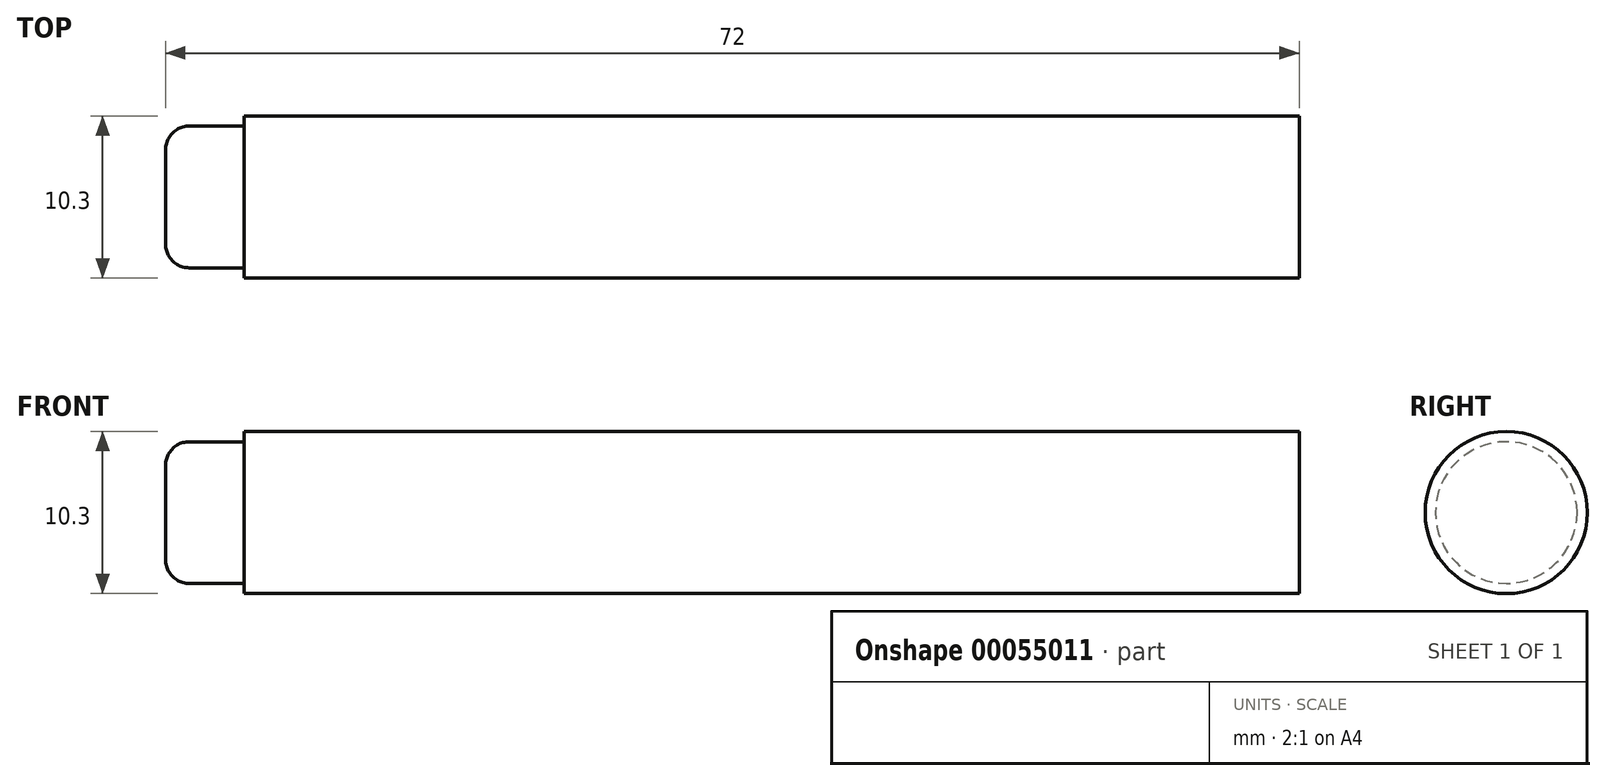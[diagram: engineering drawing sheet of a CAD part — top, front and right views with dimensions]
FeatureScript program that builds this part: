
annotation { "Feature Type Name" : "Feature", "Feature Type Description" : "" }
export const myFeature = defineFeature(function(context is Context, id is Id, definition is map)
    precondition{}
    {
        {
            var Q0;
            Q0=qCreatedBy(makeId("Front.planeOp"),FACE);
            var sketch = newSketch(context, id + "F0", { "sketchPlane" : qUnion([Q0])});
            skLineSegment(sketch, "E0", {"start": v(0, 0) * mm, "end": v(0, 3) * mm});
            skLineSegment(sketch, "E1", {"start": v(1.5, 4.5) * mm, "end": v(5, 4.5) * mm});
            skLineSegment(sketch, "E2", {"start": v(5, 4.5) * mm, "end": v(5, 5.15) * mm});
            skLineSegment(sketch, "E3", {"start": v(5, 5.15) * mm, "end": v(72, 5.15) * mm});
            skLineSegment(sketch, "E4", {"start": v(72, 5.15) * mm, "end": v(72, 0) * mm});
            skLineSegment(sketch, "E5", {"start": v(72, 0) * mm, "end": v(0, 0) * mm});
            skPoint(sketch, "E6.visualSharp", {"position": v(0, 4.5) * mm});
            skArc(sketch, "E6.filletArc", {"start": v(1.5, 4.5) * mm, "mid": v(0.44, 4.06) * mm, "end": v(0, 3) * mm});
            skSolve(sketch);
        }
        {
            var Q0;
            Q0=makeQuery(id+"F0.imprint","IMPRINT",FACE,{"disambiguationData":[TD([[makeQuery(id+"F0.imprint","IMPRINT",EDGE,{"derivedFrom":sQuery(id+"F0.wireOp",EDGE,"E0")}),-1.0]])]});
            var Q1;
            Q1=sQuery(id+"F0.wireOp",EDGE,"E5");
            revolve(context, id + "F1", {"entities" : qUnion([Q0]), "axis" : qUnion([Q1]), "revolveType" : RevolveType.FULL});
        }
    });
